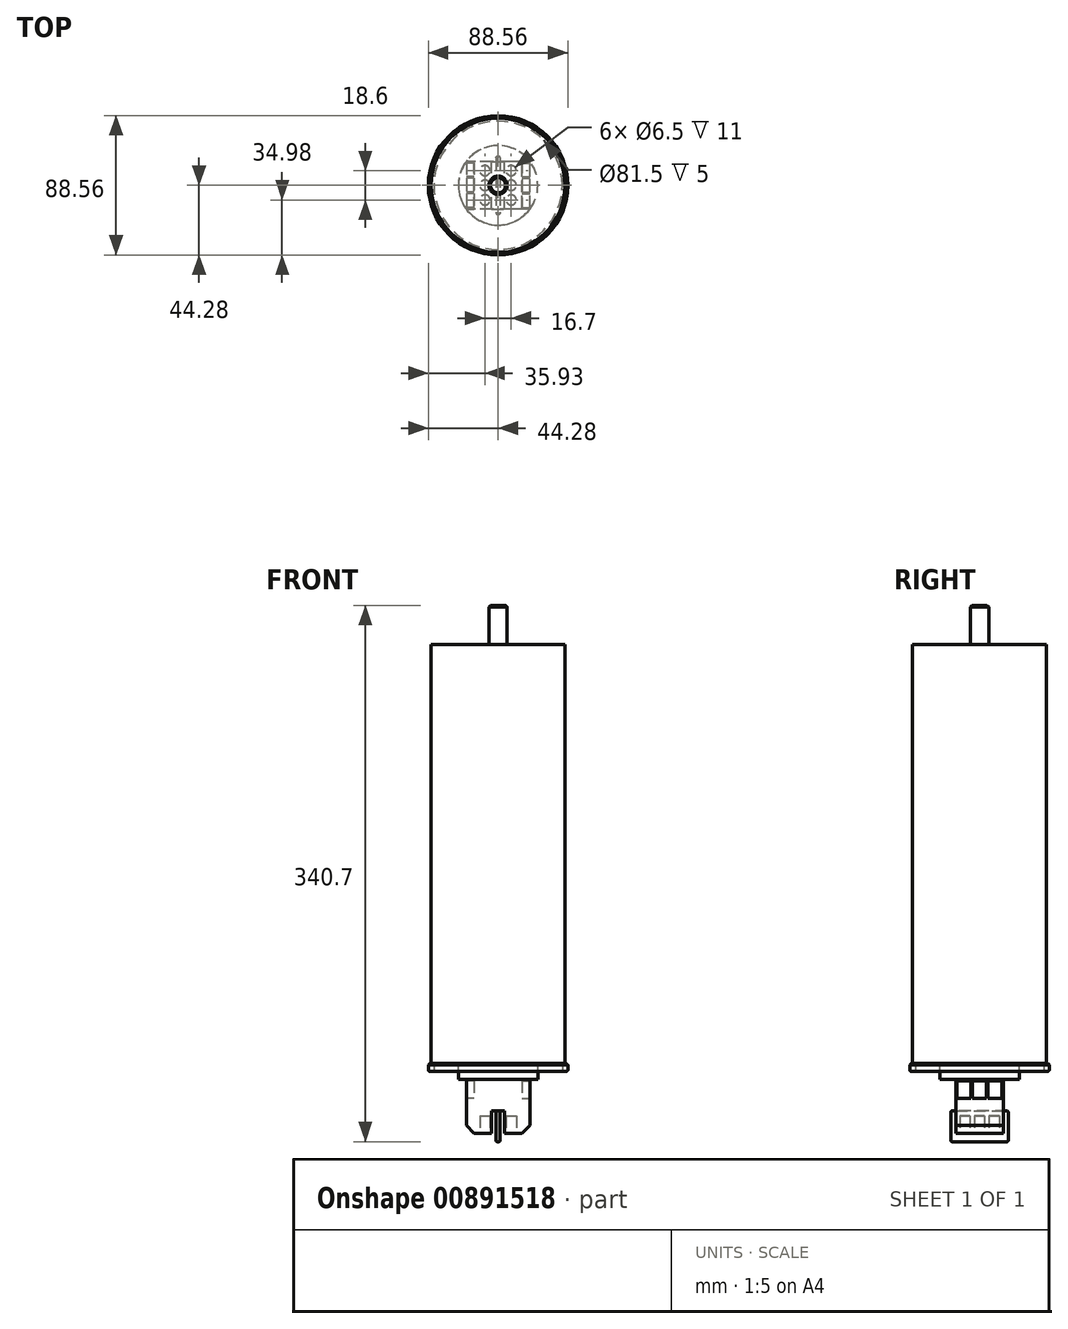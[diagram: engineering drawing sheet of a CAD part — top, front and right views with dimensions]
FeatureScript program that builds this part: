
annotation { "Feature Type Name" : "Feature", "Feature Type Description" : "" }
export const myFeature = defineFeature(function(context is Context, id is Id, definition is map)
    precondition{}
    {
        {
            var Q0;
            Q0=qCreatedBy(makeId("Top.planeOp"),FACE);
            var sketch = newSketch(context, id + "F0", { "sketchPlane" : qUnion([Q0])});
            skCircle(sketch, "E0", {"center": v(0, 0) * mm, "radius": 44.27 * mm});
            skSolve(sketch);
        }
        {
            var Q0;
            Q0 = qSketchRegion(id + "F0", true);
            extrude(context, id + "F1", {"entities" : qUnion([Q0]), "depth" : 5 * mm, "offsetDistance" : 25 * mm});
        }
        {
            var Q0;
            Q0=makeQuery(id+"F1.opExtrude","CAP_FACE",FACE,{"disambiguationData":[OSD([sQuery(id+"F0.wireOp",EDGE,"E0")])],"isStart":false});
            var sketch = newSketch(context, id + "F2", { "sketchPlane" : qUnion([Q0])});
            skCircle(sketch, "E1", {"center": v(0, 0) * mm, "radius": 42.55 * mm});
            skSolve(sketch);
        }
        {
            var Q0;
            Q0 = qSketchRegion(id + "F2", true);
            extrude(context, id + "F3", {"entities" : qUnion([Q0]), "operationType" : NewBodyOperationType.ADD, "depth" : 266 * mm, "offsetDistance" : 25 * mm});
        }
        {
            var Q0;
            Q0=makeQuery(id+"F1.opExtrude","CAP_EDGE",EDGE,{"disambiguationData":[OSD([sQuery(id+"F0.wireOp",EDGE,"E0")])],"isStart":false});
            chamfer(context, id + "F4", {"entities" : qUnion([Q0]), "width" : 1 * mm, "tangentPropagation" : true});
        }
        {
            var Q0;
            Q0=makeQuery(id+"F3.opExtrude","CAP_FACE",FACE,{"disambiguationData":[OSD([sQuery(id+"F2.wireOp",EDGE,"E1")])],"isStart":false});
            var sketch = newSketch(context, id + "F5", { "sketchPlane" : qUnion([Q0])});
            skCircle(sketch, "E2", {"center": v(0, 0) * mm, "radius": 5.8 * mm});
            skSolve(sketch);
        }
        {
            var Q0;
            Q0 = qSketchRegion(id + "F5", true);
            extrude(context, id + "F6", {"entities" : qUnion([Q0]), "operationType" : NewBodyOperationType.ADD, "depth" : 25 * mm, "offsetDistance" : 25 * mm});
        }
        {
            var Q0;
            Q0=makeQuery(id+"F6.opExtrude","CAP_EDGE",EDGE,{"disambiguationData":[OSD([sQuery(id+"F5.wireOp",EDGE,"E2")])],"isStart":false});
            chamfer(context, id + "F7", {"entities" : qUnion([Q0]), "width" : 1 * mm, "tangentPropagation" : true});
        }
        {
            var Q0;
            Q0=makeQuery(id+"F1.opExtrude","CAP_FACE",FACE,{"disambiguationData":[OSD([sQuery(id+"F0.wireOp",EDGE,"E0")])],"isStart":true});
            var sketch = newSketch(context, id + "F8", { "sketchPlane" : qUnion([Q0])});
            skCircle(sketch, "E3", {"center": v(0, 0) * mm, "radius": 40.75 * mm});
            skSolve(sketch);
        }
        {
            var Q0;
            Q0 = qSketchRegion(id + "F8", true);
            extrude(context, id + "F9", {"entities" : qUnion([Q0]), "operationType" : NewBodyOperationType.REMOVE, "oppositeDirection" : true, "depth" : 5 * mm, "offsetDistance" : 25 * mm});
        }
        {
            var Q0;
            Q0=makeQuery(id+"F9.boolean.opBoolean","COPY",FACE,{"derivedFrom":makeQuery(id+"F9.opExtrude","CAP_FACE",FACE,{"disambiguationData":[OSD([sQuery(id+"F8.wireOp",EDGE,"E3")])],"isStart":false})});
            var sketch = newSketch(context, id + "F10", { "sketchPlane" : qUnion([Q0])});
            skCircle(sketch, "E4", {"center": v(0, 0) * mm, "radius": 25.25 * mm});
            skSolve(sketch);
        }
        {
            var Q0;
            Q0 = qSketchRegion(id + "F10", true);
            extrude(context, id + "F11", {"entities" : qUnion([Q0]), "depth" : 10 * mm, "offsetDistance" : 25 * mm});
        }
        {
            var Q0;
            Q0=makeQuery(id+"F11.opExtrude","CAP_FACE",FACE,{"disambiguationData":[OSD([sQuery(id+"F10.wireOp",EDGE,"E4")])],"isStart":false});
            var sketch = newSketch(context, id + "F12", { "sketchPlane" : qUnion([Q0])});
            skLineSegment(sketch, "E5.bottom", {"start": v(20.2, 15.15) * mm, "end": v(-20.2, 15.15) * mm});
            skLineSegment(sketch, "E5.top", {"start": v(20.2, -15.15) * mm, "end": v(-20.2, -15.15) * mm});
            skLineSegment(sketch, "E5.left", {"start": v(20.2, 15.15) * mm, "end": v(20.2, -15.15) * mm});
            skLineSegment(sketch, "E5.right", {"start": v(-20.2, 15.15) * mm, "end": v(-20.2, -15.15) * mm});
            skPoint(sketch, "E5.middle", {"position": v(0, 0) * mm});
            skSolve(sketch);
        }
        {
            var Q0;
            Q0 = qSketchRegion(id + "F12", true);
            extrude(context, id + "F13", {"entities" : qUnion([Q0]), "operationType" : NewBodyOperationType.ADD, "depth" : 34.3 * mm, "offsetDistance" : 25 * mm});
        }
        {
            var Q0;
            Q0=makeQuery(id+"F13.opExtrude","SWEPT_FACE",FACE,{"disambiguationData":[OSD([sQuery(id+"F12.wireOp",EDGE,"E5.top")])]});
            var sketch = newSketch(context, id + "F14", { "sketchPlane" : qUnion([Q0])});
            skLineSegment(sketch, "E6.bottom", {"start": v(4.1, -39.3) * mm, "end": v(-4.1, -39.3) * mm});
            skLineSegment(sketch, "E6.top", {"start": v(4.1, -25.2) * mm, "end": v(-4.1, -25.2) * mm});
            skLineSegment(sketch, "E6.left", {"start": v(4.1, -39.3) * mm, "end": v(4.1, -25.2) * mm});
            skLineSegment(sketch, "E6.right", {"start": v(-4.1, -39.3) * mm, "end": v(-4.1, -25.2) * mm});
            skSolve(sketch);
        }
        {
            var Q0;
            Q0 = qSketchRegion(id + "F14", true);
            extrude(context, id + "F15", {"entities" : qUnion([Q0]), "operationType" : NewBodyOperationType.REMOVE, "endBound" : BoundingType.THROUGH_ALL, "oppositeDirection" : true, "depth" : 25 * mm, "offsetDistance" : 25 * mm});
        }
        {
            var Q0;
            Q0=makeQuery(id+"F13.opExtrude","CAP_EDGE",EDGE,{"disambiguationData":[OSD([sQuery(id+"F12.wireOp",EDGE,"E5.right")])],"isStart":false});
            var Q1;
            Q1=makeQuery(id+"F13.opExtrude","CAP_EDGE",EDGE,{"disambiguationData":[OSD([sQuery(id+"F12.wireOp",EDGE,"E5.left")])],"isStart":false});
            chamfer(context, id + "F16", {"entities" : qUnion([Q0, Q1]), "width" : 5 * mm, "tangentPropagation" : true});
        }
        {
            var Q0;
            {var subQ0=sQuery(id+"F12.wireOp",EDGE,"E5.bottom");var subQ1=sQuery(id+"F12.wireOp",EDGE,"E5.right");var subQ2=sQuery(id+"F12.wireOp",EDGE,"E5.top");Q0=makeQuery(id+"F15.boolean.opBoolean","SPLIT",FACE,{"disambiguationData":[TD([makeQuery(id+"F13.opExtrude","SWEPT_FACE",FACE,{"disambiguationData":[OSD([subQ1])]})])],"derivedFrom":makeQuery(id+"F13.opExtrude","CAP_FACE",FACE,{"disambiguationData":[OSD([subQ0,subQ2,sQuery(id+"F12.wireOp",EDGE,"E5.left"),subQ1])],"isStart":false})});}
            var sketch = newSketch(context, id + "F17", { "sketchPlane" : qUnion([Q0])});
            skCircle(sketch, "E7", {"center": v(-8.35, 0) * mm, "radius": 3.25 * mm});
            skCircle(sketch, "E8", {"center": v(-8.35, 9.3) * mm, "radius": 3.25 * mm});
            skCircle(sketch, "E9", {"center": v(-8.35, -9.3) * mm, "radius": 3.25 * mm});
            skCircle(sketch, "E10.MirrorC", {"center": v(8.35, 0) * mm, "radius": 3.25 * mm});
            skCircle(sketch, "E11.MirrorC", {"center": v(8.35, 9.3) * mm, "radius": 3.25 * mm});
            skCircle(sketch, "E12.MirrorC", {"center": v(8.35, -9.3) * mm, "radius": 3.25 * mm});
            skSolve(sketch);
        }
        {
            var Q0;
            Q0 = qSketchRegion(id + "F17", true);
            extrude(context, id + "F18", {"entities" : qUnion([Q0]), "operationType" : NewBodyOperationType.REMOVE, "oppositeDirection" : true, "depth" : 11 * mm, "offsetDistance" : 25 * mm});
        }
        {
            var Q0;
            Q0=makeQuery(id+"F13.opExtrude","SWEPT_FACE",FACE,{"disambiguationData":[OSD([sQuery(id+"F12.wireOp",EDGE,"E5.right")])]});
            var sketch = newSketch(context, id + "F19", { "sketchPlane" : qUnion([Q0])});
            skLineSegment(sketch, "E13.bottom", {"start": v(-4.4, -6.2) * mm, "end": v(4.4, -6.2) * mm});
            skLineSegment(sketch, "E13.top", {"start": v(-4.4, -17.2) * mm, "end": v(4.4, -17.2) * mm});
            skLineSegment(sketch, "E13.left", {"start": v(-4.4, -6.2) * mm, "end": v(-4.4, -17.2) * mm});
            skLineSegment(sketch, "E13.right", {"start": v(4.4, -6.2) * mm, "end": v(4.4, -17.2) * mm});
            skPoint(sketch, "E13.middle", {"position": v(0, -11.7) * mm});
            skLineSegment(sketch, "E14.bottom", {"start": v(-14.2, -6.2) * mm, "end": v(-5.4, -6.2) * mm});
            skLineSegment(sketch, "E14.top", {"start": v(-14.2, -17.2) * mm, "end": v(-5.4, -17.2) * mm});
            skLineSegment(sketch, "E14.left", {"start": v(-14.2, -6.2) * mm, "end": v(-14.2, -17.2) * mm});
            skLineSegment(sketch, "E14.right", {"start": v(-5.4, -6.2) * mm, "end": v(-5.4, -17.2) * mm});
            skPoint(sketch, "E14.middle", {"position": v(-9.8, -11.7) * mm});
            skLineSegment(sketch, "E15.bottom", {"start": v(5.4, -6.2) * mm, "end": v(14.2, -6.2) * mm});
            skLineSegment(sketch, "E15.top", {"start": v(5.4, -17.2) * mm, "end": v(14.2, -17.2) * mm});
            skLineSegment(sketch, "E15.left", {"start": v(5.4, -6.2) * mm, "end": v(5.4, -17.2) * mm});
            skLineSegment(sketch, "E15.right", {"start": v(14.2, -6.2) * mm, "end": v(14.2, -17.2) * mm});
            skPoint(sketch, "E15.middle", {"position": v(9.8, -11.7) * mm});
            skSolve(sketch);
        }
        {
            var Q0;
            Q0 = qSketchRegion(id + "F19", true);
            extrude(context, id + "F20", {"entities" : qUnion([Q0]), "operationType" : NewBodyOperationType.REMOVE, "oppositeDirection" : true, "depth" : 5 * mm, "offsetDistance" : 25 * mm});
        }
        {
            var Q0;
            Q0=makeQuery(id+"F13.opExtrude","SWEPT_FACE",FACE,{"disambiguationData":[OSD([sQuery(id+"F12.wireOp",EDGE,"E5.left")])]});
            var sketch = newSketch(context, id + "F21", { "sketchPlane" : qUnion([Q0])});
            skLineSegment(sketch, "E16.bottom", {"start": v(-4.4, -6.2) * mm, "end": v(4.4, -6.2) * mm});
            skLineSegment(sketch, "E16.top", {"start": v(-4.4, -17.2) * mm, "end": v(4.4, -17.2) * mm});
            skLineSegment(sketch, "E16.left", {"start": v(-4.4, -6.2) * mm, "end": v(-4.4, -17.2) * mm});
            skLineSegment(sketch, "E16.right", {"start": v(4.4, -6.2) * mm, "end": v(4.4, -17.2) * mm});
            skPoint(sketch, "E16.middle", {"position": v(0, -11.7) * mm});
            skLineSegment(sketch, "E17.bottom", {"start": v(-14.2, -6.2) * mm, "end": v(-5.4, -6.2) * mm});
            skLineSegment(sketch, "E17.top", {"start": v(-14.2, -17.2) * mm, "end": v(-5.4, -17.2) * mm});
            skLineSegment(sketch, "E17.left", {"start": v(-14.2, -6.2) * mm, "end": v(-14.2, -17.2) * mm});
            skLineSegment(sketch, "E17.right", {"start": v(-5.4, -6.2) * mm, "end": v(-5.4, -17.2) * mm});
            skPoint(sketch, "E17.middle", {"position": v(-9.8, -11.7) * mm});
            skLineSegment(sketch, "E18.bottom", {"start": v(5.4, -6.2) * mm, "end": v(14.2, -6.2) * mm});
            skLineSegment(sketch, "E18.top", {"start": v(5.4, -17.2) * mm, "end": v(14.2, -17.2) * mm});
            skLineSegment(sketch, "E18.left", {"start": v(5.4, -6.2) * mm, "end": v(5.4, -17.2) * mm});
            skLineSegment(sketch, "E18.right", {"start": v(14.2, -6.2) * mm, "end": v(14.2, -17.2) * mm});
            skPoint(sketch, "E18.middle", {"position": v(9.8, -11.7) * mm});
            skSolve(sketch);
        }
        {
            var Q0;
            Q0 = qSketchRegion(id + "F21", true);
            extrude(context, id + "F22", {"entities" : qUnion([Q0]), "operationType" : NewBodyOperationType.REMOVE, "oppositeDirection" : true, "depth" : 5 * mm, "offsetDistance" : 25 * mm});
        }
        {
            var Q0;
            Q0=makeQuery(id+"F15.boolean.opBoolean","COPY",FACE,{"derivedFrom":makeQuery(id+"F15.opExtrude","SWEPT_FACE",FACE,{"disambiguationData":[OSD([sQuery(id+"F14.wireOp",EDGE,"E6.top")])]})});
            var sketch = newSketch(context, id + "F23", { "sketchPlane" : qUnion([Q0])});
            skLineSegment(sketch, "E19.bottom", {"start": v(-1.35, -18.25) * mm, "end": v(1.35, -18.25) * mm});
            skLineSegment(sketch, "E19.top", {"start": v(-1.35, 18.25) * mm, "end": v(1.35, 18.25) * mm});
            skLineSegment(sketch, "E19.left", {"start": v(-1.35, -18.25) * mm, "end": v(-1.35, 18.25) * mm});
            skLineSegment(sketch, "E19.right", {"start": v(1.35, -18.25) * mm, "end": v(1.35, 18.25) * mm});
            skPoint(sketch, "E19.middle", {"position": v(0, 0) * mm});
            skSolve(sketch);
        }
        {
            var Q0;
            Q0 = qSketchRegion(id + "F23", true);
            extrude(context, id + "F24", {"entities" : qUnion([Q0]), "depth" : 19.5 * mm, "offsetDistance" : 25 * mm});
        }
        {
            var Q0;
            Q0=makeQuery(id+"F24.opExtrude","SWEPT_FACE",FACE,{"disambiguationData":[OSD([sQuery(id+"F23.wireOp",EDGE,"E19.top")])]});
            var Q1;
            Q1=makeQuery(id+"F24.opExtrude","SWEPT_FACE",FACE,{"disambiguationData":[OSD([sQuery(id+"F23.wireOp",EDGE,"E19.bottom")])]});
            var Q2;
            Q2=makeQuery(id+"F24.opExtrude","CAP_FACE",FACE,{"disambiguationData":[OSD([sQuery(id+"F23.wireOp",EDGE,"E19.bottom"),sQuery(id+"F23.wireOp",EDGE,"E19.top"),sQuery(id+"F23.wireOp",EDGE,"E19.left"),sQuery(id+"F23.wireOp",EDGE,"E19.right")])],"isStart":false});
            fillet(context, id + "F25", {"entities" : qUnion([Q0, Q1, Q2]), "radius" : .8 * mm, "tangentPropagation" : true, "allowEdgeOverflow" : false});
        }
        {
            var Q0;
            Q0=makeQuery(id+"F1.opExtrude","CAP_EDGE",EDGE,{"disambiguationData":[OSD([sQuery(id+"F0.wireOp",EDGE,"E0")])],"isStart":true});
            var Q1;
            Q1=makeQuery(id+"F9.boolean.opBoolean","COPY",EDGE,{"derivedFrom":makeQuery(id+"F9.opExtrude","CAP_EDGE",EDGE,{"disambiguationData":[OSD([sQuery(id+"F8.wireOp",EDGE,"E3")])],"isStart":true})});
            fillet(context, id + "F26", {"entities" : qUnion([Q0, Q1]), "radius" : .8 * mm, "tangentPropagation" : true, "allowEdgeOverflow" : false});
        }
    });
